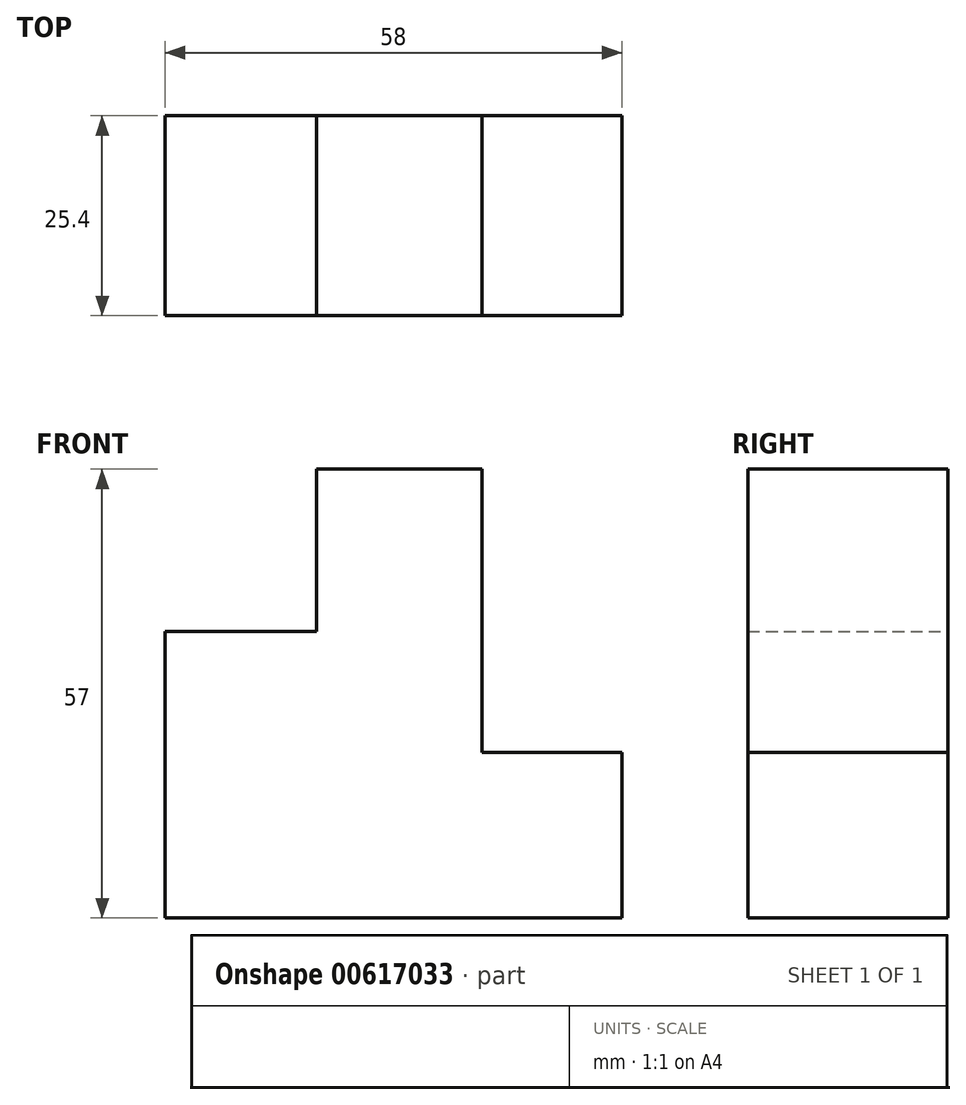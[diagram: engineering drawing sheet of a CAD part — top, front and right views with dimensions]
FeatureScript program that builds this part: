
annotation { "Feature Type Name" : "Feature", "Feature Type Description" : "" }
export const myFeature = defineFeature(function(context is Context, id is Id, definition is map)
    precondition{}
    {
        {
            var Q0;
            Q0=qCreatedBy(makeId("Front.planeOp"),FACE);
            var sketch = newSketch(context, id + "F0", { "sketchPlane" : qUnion([Q0])});
            skLineSegment(sketch, "E0", {"start": v(-32.71, 15.38) * mm, "end": v(-32.71, -21) * mm});
            skLineSegment(sketch, "E1", {"start": v(-32.71, -21) * mm, "end": v(-32.71, 15.38) * mm});
            skLineSegment(sketch, "E2", {"start": v(-32.71, 15.38) * mm, "end": v(-13.49, 15.38) * mm});
            skLineSegment(sketch, "E3", {"start": v(-13.49, 15.38) * mm, "end": v(-13.49, 36) * mm});
            skLineSegment(sketch, "E4", {"start": v(-13.49, 36) * mm, "end": v(7.51, 36) * mm});
            skLineSegment(sketch, "E5", {"start": v(7.51, 36) * mm, "end": v(7.51, 0) * mm});
            skLineSegment(sketch, "E6", {"start": v(7.51, 0) * mm, "end": v(25.29, 0) * mm});
            skLineSegment(sketch, "E7", {"start": v(25.29, 0) * mm, "end": v(25.29, -21) * mm});
            skLineSegment(sketch, "E8", {"start": v(25.29, -21) * mm, "end": v(-32.71, -21) * mm});
            skSolve(sketch);
        }
        {
            var Q0;
            Q0 = qSketchRegion(id + "F0", true);
            extrude(context, id + "F1", {"entities" : qUnion([Q0]), "depth" : 25.4 * mm, "offsetDistance" : 25.4 * mm});
        }
    });
